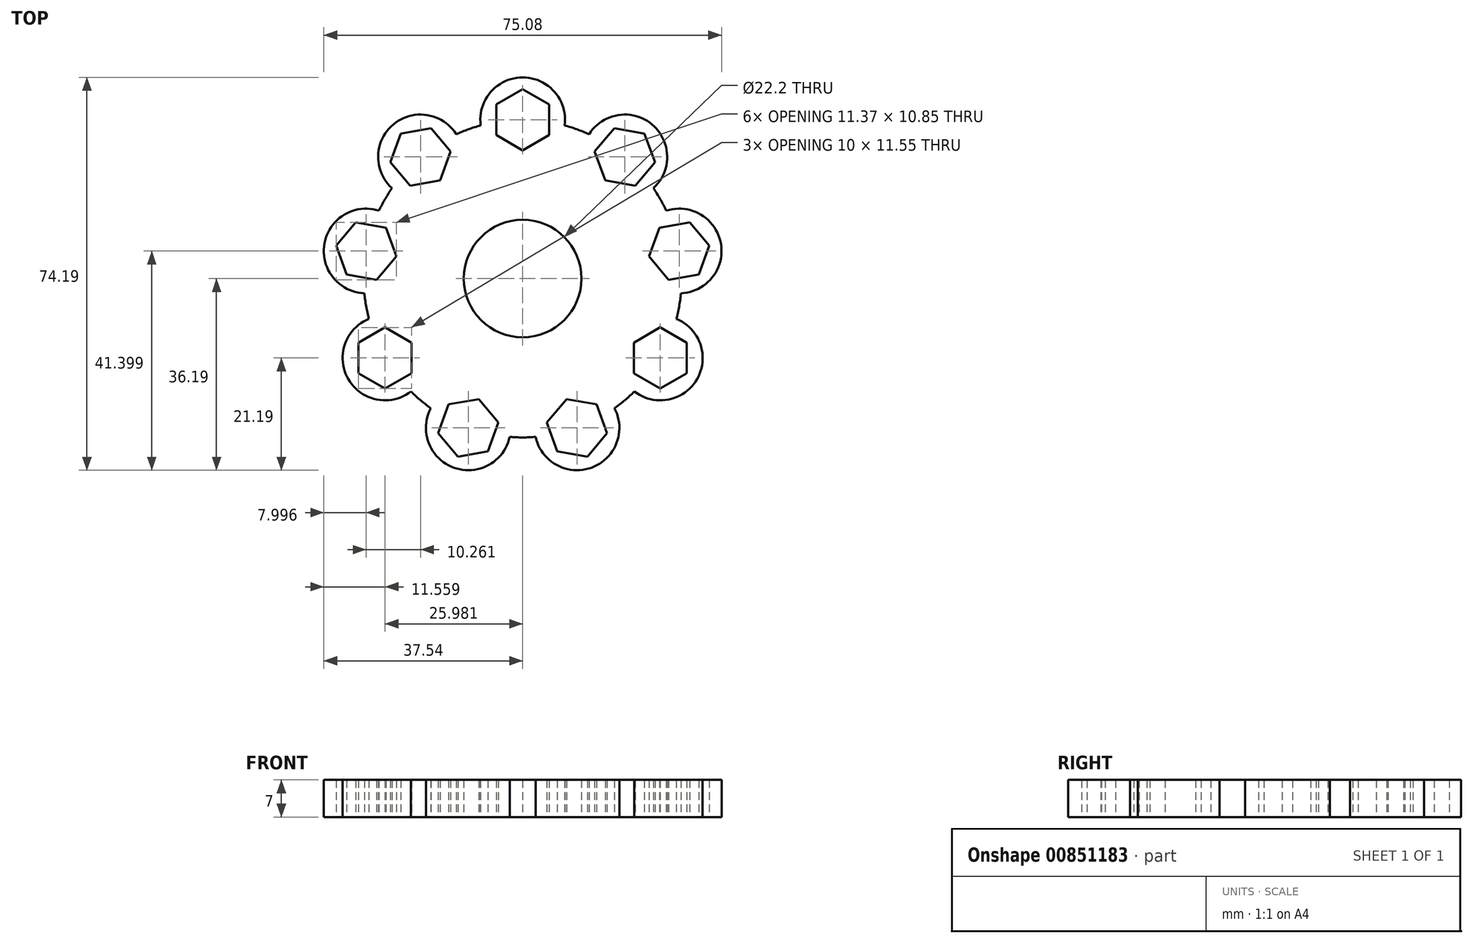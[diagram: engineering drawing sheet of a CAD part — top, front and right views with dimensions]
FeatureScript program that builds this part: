
annotation { "Feature Type Name" : "Feature", "Feature Type Description" : "" }
export const myFeature = defineFeature(function(context is Context, id is Id, definition is map)
    precondition{}
    {
        {
            var Q0;
            Q0=qCreatedBy(makeId("Top.planeOp"),FACE);
            var sketch = newSketch(context, id + "F0", { "sketchPlane" : qUnion([Q0])});
            skCircle(sketch, "E0", {"center": v(0, 0) * mm, "radius": 11.1 * mm});
            skCircle(sketch, "E1", {"center": v(0, 0) * mm, "radius": 30 * mm});
            skCircle(sketch, "E2.cCircle", {"center": v(0, 30) * mm, "radius": 5 * mm, "construction": true});
            skLineSegment(sketch, "E2.0", {"start": v(0, 35.77) * mm, "end": v(5, 32.89) * mm});
            skLineSegment(sketch, "E2.1", {"start": v(5, 32.89) * mm, "end": v(5, 27.11) * mm});
            skLineSegment(sketch, "E2.2", {"start": v(5, 27.11) * mm, "end": v(0, 24.23) * mm});
            skLineSegment(sketch, "E2.3", {"start": v(0, 24.23) * mm, "end": v(-5, 27.11) * mm});
            skLineSegment(sketch, "E2.4", {"start": v(-5, 27.11) * mm, "end": v(-5, 32.89) * mm});
            skLineSegment(sketch, "E2.5", {"start": v(-5, 32.89) * mm, "end": v(0, 35.77) * mm});
            skPoint(sketch, "E2.0.midPoint", {"position": v(2.5, 34.33) * mm});
            skLineSegment(sketch, "E3.1.0", {"start": v(-23, 27.4) * mm, "end": v(-17.3, 28.4) * mm});
            skLineSegment(sketch, "E3.1.1", {"start": v(-17.3, 28.4) * mm, "end": v(-13.6, 23.98) * mm});
            skLineSegment(sketch, "E3.1.2", {"start": v(-13.6, 23.98) * mm, "end": v(-15.57, 18.56) * mm});
            skLineSegment(sketch, "E3.1.3", {"start": v(-15.57, 18.56) * mm, "end": v(-21.26, 17.56) * mm});
            skLineSegment(sketch, "E3.1.4", {"start": v(-21.26, 17.56) * mm, "end": v(-24.97, 21.98) * mm});
            skLineSegment(sketch, "E3.1.5", {"start": v(-24.97, 21.98) * mm, "end": v(-23, 27.4) * mm});
            skCircle(sketch, "E3.1.6", {"center": v(-19.28, 22.98) * mm, "radius": 5 * mm, "construction": true});
            skLineSegment(sketch, "E3.2.0", {"start": v(-35.23, 6.21) * mm, "end": v(-31.52, 10.63) * mm});
            skLineSegment(sketch, "E3.2.1", {"start": v(-31.52, 10.63) * mm, "end": v(-25.83, 9.63) * mm});
            skLineSegment(sketch, "E3.2.2", {"start": v(-25.83, 9.63) * mm, "end": v(-23.86, 4.2) * mm});
            skLineSegment(sketch, "E3.2.3", {"start": v(-23.86, 4.2) * mm, "end": v(-27.57, -0.22) * mm});
            skLineSegment(sketch, "E3.2.4", {"start": v(-27.57, -0.22) * mm, "end": v(-33.26, 0.79) * mm});
            skLineSegment(sketch, "E3.2.5", {"start": v(-33.26, 0.79) * mm, "end": v(-35.23, 6.21) * mm});
            skCircle(sketch, "E3.2.6", {"center": v(-29.54, 5.2) * mm, "radius": 5 * mm, "construction": true});
            skLineSegment(sketch, "E4.1.3.0", {"start": v(-30.98, -17.89) * mm, "end": v(-30.98, -12.11) * mm});
            skLineSegment(sketch, "E4.3.3.0", {"start": v(-30.98, -12.11) * mm, "end": v(-25.98, -9.23) * mm});
            skLineSegment(sketch, "E4.6.3.0", {"start": v(-25.98, -9.23) * mm, "end": v(-20.98, -12.11) * mm});
            skLineSegment(sketch, "E4.9.3.0", {"start": v(-20.98, -12.11) * mm, "end": v(-20.98, -17.89) * mm});
            skLineSegment(sketch, "E4.12.3.0", {"start": v(-20.98, -17.89) * mm, "end": v(-25.98, -20.77) * mm});
            skLineSegment(sketch, "E4.15.3.0", {"start": v(-25.98, -20.77) * mm, "end": v(-30.98, -17.89) * mm});
            skCircle(sketch, "E4.18.3.0", {"center": v(-25.98, -15) * mm, "radius": 5 * mm, "construction": true});
            skLineSegment(sketch, "E4.1.4.0", {"start": v(-12.24, -33.62) * mm, "end": v(-15.95, -29.2) * mm});
            skLineSegment(sketch, "E4.3.4.0", {"start": v(-15.95, -29.2) * mm, "end": v(-13.97, -23.77) * mm});
            skLineSegment(sketch, "E4.6.4.0", {"start": v(-13.97, -23.77) * mm, "end": v(-8.29, -22.77) * mm});
            skLineSegment(sketch, "E4.9.4.0", {"start": v(-8.29, -22.77) * mm, "end": v(-4.57, -27.19) * mm});
            skLineSegment(sketch, "E4.12.4.0", {"start": v(-4.57, -27.19) * mm, "end": v(-6.55, -32.61) * mm});
            skLineSegment(sketch, "E4.15.4.0", {"start": v(-6.55, -32.61) * mm, "end": v(-12.24, -33.62) * mm});
            skCircle(sketch, "E4.18.4.0", {"center": v(-10.26, -28.2) * mm, "radius": 5 * mm, "construction": true});
            skLineSegment(sketch, "E4.1.5.0", {"start": v(12.24, -33.62) * mm, "end": v(6.55, -32.61) * mm});
            skLineSegment(sketch, "E4.3.5.0", {"start": v(6.55, -32.61) * mm, "end": v(4.57, -27.19) * mm});
            skLineSegment(sketch, "E4.6.5.0", {"start": v(4.57, -27.19) * mm, "end": v(8.29, -22.77) * mm});
            skLineSegment(sketch, "E4.9.5.0", {"start": v(8.29, -22.77) * mm, "end": v(13.97, -23.77) * mm});
            skLineSegment(sketch, "E4.12.5.0", {"start": v(13.97, -23.77) * mm, "end": v(15.95, -29.2) * mm});
            skLineSegment(sketch, "E4.15.5.0", {"start": v(15.95, -29.2) * mm, "end": v(12.24, -33.62) * mm});
            skCircle(sketch, "E4.18.5.0", {"center": v(10.26, -28.2) * mm, "radius": 5 * mm, "construction": true});
            skLineSegment(sketch, "E4.1.6.0", {"start": v(30.98, -17.89) * mm, "end": v(25.98, -20.77) * mm});
            skLineSegment(sketch, "E4.3.6.0", {"start": v(25.98, -20.77) * mm, "end": v(20.98, -17.89) * mm});
            skLineSegment(sketch, "E4.6.6.0", {"start": v(20.98, -17.89) * mm, "end": v(20.98, -12.11) * mm});
            skLineSegment(sketch, "E4.9.6.0", {"start": v(20.98, -12.11) * mm, "end": v(25.98, -9.23) * mm});
            skLineSegment(sketch, "E4.12.6.0", {"start": v(25.98, -9.23) * mm, "end": v(30.98, -12.11) * mm});
            skLineSegment(sketch, "E4.15.6.0", {"start": v(30.98, -12.11) * mm, "end": v(30.98, -17.89) * mm});
            skCircle(sketch, "E4.18.6.0", {"center": v(25.98, -15) * mm, "radius": 5 * mm, "construction": true});
            skLineSegment(sketch, "E4.1.7.0", {"start": v(35.23, 6.21) * mm, "end": v(33.26, 0.79) * mm});
            skLineSegment(sketch, "E4.3.7.0", {"start": v(33.26, 0.79) * mm, "end": v(27.57, -0.22) * mm});
            skLineSegment(sketch, "E4.6.7.0", {"start": v(27.57, -0.22) * mm, "end": v(23.86, 4.2) * mm});
            skLineSegment(sketch, "E4.9.7.0", {"start": v(23.86, 4.2) * mm, "end": v(25.83, 9.63) * mm});
            skLineSegment(sketch, "E4.12.7.0", {"start": v(25.83, 9.63) * mm, "end": v(31.52, 10.63) * mm});
            skLineSegment(sketch, "E4.15.7.0", {"start": v(31.52, 10.63) * mm, "end": v(35.23, 6.21) * mm});
            skCircle(sketch, "E4.18.7.0", {"center": v(29.54, 5.2) * mm, "radius": 5 * mm, "construction": true});
            skLineSegment(sketch, "E4.1.8.0", {"start": v(23, 27.4) * mm, "end": v(24.97, 21.98) * mm});
            skLineSegment(sketch, "E4.3.8.0", {"start": v(24.97, 21.98) * mm, "end": v(21.26, 17.56) * mm});
            skLineSegment(sketch, "E4.6.8.0", {"start": v(21.26, 17.56) * mm, "end": v(15.57, 18.56) * mm});
            skLineSegment(sketch, "E4.9.8.0", {"start": v(15.57, 18.56) * mm, "end": v(13.6, 23.98) * mm});
            skLineSegment(sketch, "E4.12.8.0", {"start": v(13.6, 23.98) * mm, "end": v(17.3, 28.4) * mm});
            skLineSegment(sketch, "E4.15.8.0", {"start": v(17.3, 28.4) * mm, "end": v(23, 27.4) * mm});
            skCircle(sketch, "E4.18.8.0", {"center": v(19.28, 22.98) * mm, "radius": 5 * mm, "construction": true});
            skCircle(sketch, "E5", {"center": v(0, 30) * mm, "radius": 8 * mm});
            skCircle(sketch, "E6.1.0", {"center": v(-19.28, 22.98) * mm, "radius": 8 * mm});
            skCircle(sketch, "E6.2.0", {"center": v(-29.54, 5.2) * mm, "radius": 8 * mm});
            skCircle(sketch, "E6.3.0", {"center": v(-25.98, -15) * mm, "radius": 8 * mm});
            skCircle(sketch, "E6.4.0", {"center": v(-10.26, -28.2) * mm, "radius": 8 * mm});
            skCircle(sketch, "E6.5.0", {"center": v(10.26, -28.2) * mm, "radius": 8 * mm});
            skCircle(sketch, "E6.6.0", {"center": v(25.98, -15) * mm, "radius": 8 * mm});
            skCircle(sketch, "E6.7.0", {"center": v(29.54, 5.2) * mm, "radius": 8 * mm});
            skCircle(sketch, "E6.8.0", {"center": v(19.28, 22.98) * mm, "radius": 8 * mm});
            skArc(sketch, "E7", {"start": v(7.93, 28.93) * mm, "mid": v(9.42, 25.88) * mm, "end": v(12.52, 27.26) * mm});
            skArc(sketch, "E8.1.0", {"start": v(-12.52, 27.26) * mm, "mid": v(-9.42, 25.88) * mm, "end": v(-7.93, 28.93) * mm});
            skArc(sketch, "E8.2.0", {"start": v(-27.12, 12.83) * mm, "mid": v(-23.85, 13.77) * mm, "end": v(-24.67, 17.07) * mm});
            skArc(sketch, "E8.3.0", {"start": v(-29.02, -7.6) * mm, "mid": v(-27.12, -4.78) * mm, "end": v(-29.87, -2.78) * mm});
            skArc(sketch, "E8.4.0", {"start": v(-17.35, -24.48) * mm, "mid": v(-17.7, -21.1) * mm, "end": v(-21.1, -21.33) * mm});
            skArc(sketch, "E8.5.0", {"start": v(2.45, -29.9) * mm, "mid": v(0, -27.54) * mm, "end": v(-2.45, -29.9) * mm});
            skArc(sketch, "E8.6.0", {"start": v(21.1, -21.33) * mm, "mid": v(17.7, -21.1) * mm, "end": v(17.35, -24.48) * mm});
            skArc(sketch, "E8.7.0", {"start": v(29.87, -2.78) * mm, "mid": v(27.12, -4.78) * mm, "end": v(29.02, -7.6) * mm});
            skArc(sketch, "E8.8.0", {"start": v(24.67, 17.07) * mm, "mid": v(23.85, 13.77) * mm, "end": v(27.12, 12.83) * mm});
            skSolve(sketch);
        }
        {
            var Q0;
            Q0 = qSketchRegion(id + "F0", true);
            var Q1;
            Q1=makeQuery(id+"F0.imprint","IMPRINT",FACE,{"disambiguationData":[TD([[makeQuery(id+"F0.imprint","IMPRINT",EDGE,{"derivedFrom":sQuery(id+"F0.wireOp",EDGE,"E0")}),-1.0]])]});
            extrude(context, id + "F1", {"entities" : qUnion([Q0, Q1]), "depth" : 7 * mm, "offsetDistance" : 25 * mm});
        }
    });
